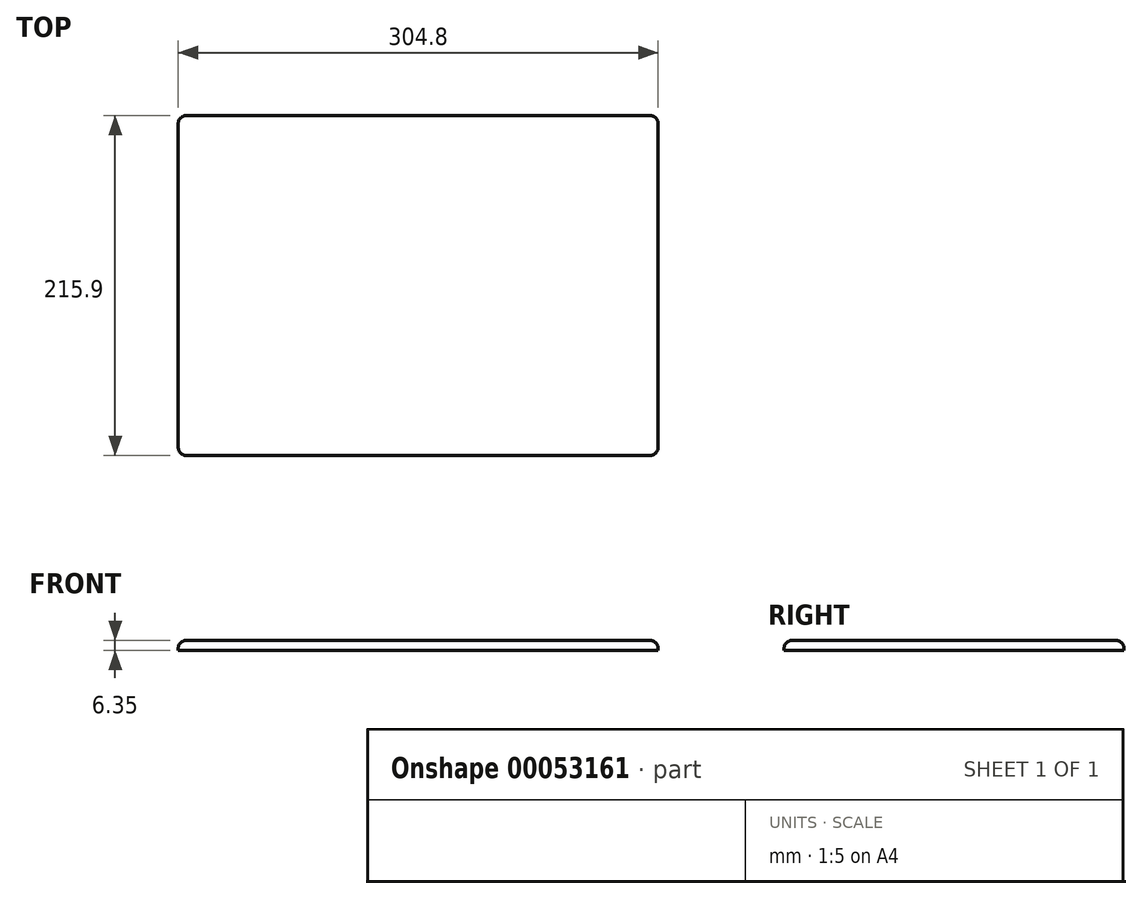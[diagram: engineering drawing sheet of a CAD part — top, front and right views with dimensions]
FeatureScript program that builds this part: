
annotation { "Feature Type Name" : "Feature", "Feature Type Description" : "" }
export const myFeature = defineFeature(function(context is Context, id is Id, definition is map)
    precondition{}
    {
        {
            var Q0;
            Q0=qCreatedBy(makeId("Top.planeOp"),FACE);
            var sketch = newSketch(context, id + "F0", { "sketchPlane" : qUnion([Q0])});
            skLineSegment(sketch, "E0.bottom", {"start": v(-152.02, 132.04) * mm, "end": v(152.78, 132.04) * mm});
            skLineSegment(sketch, "E0.top", {"start": v(-152.02, -83.86) * mm, "end": v(152.78, -83.86) * mm});
            skLineSegment(sketch, "E0.left", {"start": v(-152.02, 132.04) * mm, "end": v(-152.02, -83.86) * mm});
            skLineSegment(sketch, "E0.right", {"start": v(152.78, 132.04) * mm, "end": v(152.78, -83.86) * mm});
            skSolve(sketch);
        }
        {
            var Q0;
            Q0 = qSketchRegion(id + "F0", true);
            extrude(context, id + "F1", {"entities" : qUnion([Q0]), "depth" : 6.35 * mm});
        }
        {
            var Q0;
            Q0=makeQuery(id+"F1.opExtrude","SWEPT_EDGE",EDGE,{"disambiguationData":[OSD([sQuery(id+"F0.wireOp",EDGE,"E0.top"),sQuery(id+"F0.wireOp",EDGE,"E0.right")])]});
            var Q1;
            Q1=makeQuery(id+"F1.opExtrude","CAP_EDGE",EDGE,{"disambiguationData":[OSD([sQuery(id+"F0.wireOp",EDGE,"E0.top")])],"isStart":false});
            var Q2;
            Q2=makeQuery(id+"F1.opExtrude","CAP_EDGE",EDGE,{"disambiguationData":[OSD([sQuery(id+"F0.wireOp",EDGE,"E0.left")])],"isStart":false});
            var Q3;
            Q3=makeQuery(id+"F1.opExtrude","CAP_EDGE",EDGE,{"disambiguationData":[OSD([sQuery(id+"F0.wireOp",EDGE,"E0.bottom")])],"isStart":false});
            var Q4;
            Q4=makeQuery(id+"F1.opExtrude","CAP_EDGE",EDGE,{"disambiguationData":[OSD([sQuery(id+"F0.wireOp",EDGE,"E0.right")])],"isStart":false});
            fillet(context, id + "F2", {"entities" : qUnion([Q0, Q1, Q2, Q3, Q4]), "radius" : 5.08 * mm, "tangentPropagation" : true, "allowEdgeOverflow" : false});
        }
        {
            var Q0;
            Q0=makeQuery(id+"F2.opFillet","BLEND_EDGE",EDGE,{"blendedFrom":[makeQuery(id+"F1.opExtrude","CAP_EDGE",EDGE,{"disambiguationData":[OSD([sQuery(id+"F0.wireOp",EDGE,"E0.bottom")])],"isStart":false}),makeQuery(id+"F1.opExtrude","CAP_EDGE",EDGE,{"disambiguationData":[OSD([sQuery(id+"F0.wireOp",EDGE,"E0.right")])],"isStart":false})],"blendedInto":[]});
            var Q1;
            Q1=makeQuery(id+"F2.opFillet","BLEND_EDGE",EDGE,{"blendedFrom":[makeQuery(id+"F1.opExtrude","CAP_EDGE",EDGE,{"disambiguationData":[OSD([sQuery(id+"F0.wireOp",EDGE,"E0.bottom")])],"isStart":false}),makeQuery(id+"F1.opExtrude","CAP_EDGE",EDGE,{"disambiguationData":[OSD([sQuery(id+"F0.wireOp",EDGE,"E0.left")])],"isStart":false})],"blendedInto":[]});
            var Q2;
            Q2=makeQuery(id+"F2.opFillet","BLEND_EDGE",EDGE,{"blendedFrom":[makeQuery(id+"F1.opExtrude","CAP_EDGE",EDGE,{"disambiguationData":[OSD([sQuery(id+"F0.wireOp",EDGE,"E0.top")])],"isStart":false}),makeQuery(id+"F1.opExtrude","CAP_EDGE",EDGE,{"disambiguationData":[OSD([sQuery(id+"F0.wireOp",EDGE,"E0.left")])],"isStart":false})],"blendedInto":[]});
            fillet(context, id + "F3", {"entities" : qUnion([Q0, Q1, Q2]), "radius" : 5.08 * mm, "tangentPropagation" : true, "allowEdgeOverflow" : false});
        }
    });
